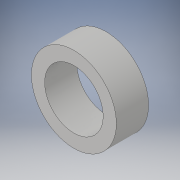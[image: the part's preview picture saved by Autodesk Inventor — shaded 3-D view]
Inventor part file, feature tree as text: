
AUTODESK INVENTOR PART (.ipt)
format: ipt  version: 2021 (Build 250183000, 183)  size: 121,344 bytes
history: native  units: mm
features: other x14, extrude x1, sketch x1
ambient origin geometry x8: Origin, YZ Plane, XZ Plane, XY Plane, X Axis, Y Axis, Z Axis, Center Point
bodies: Solid1 (feature_tree)
feature tree (16):
  extrude  "Extrusion1"  TaperAngle=0.0deg  [1 undecoded]
  other  "to_base_XY"
  other  "to_base_YZ"
  other  "to_base_ZX"
  other  "to_base_X"
  other  "to_base_Y"
  other  "to_base_Z"
  other  "to_base_Center"
  other  "to_nut_XY"
  other  "to_nut_YZ"
  other  "to_nut_ZX"
  other  "to_nut_X"
  other  "to_nut_Y"
  other  "to_nut_Z"
  other  "to_nut_Center"
  sketch  "Sketch_1"  dims[d0=5.5mm d1=0.0mm d2=0.0mm d3=0.0mm]
note: 1 required parameter value undecoded (feature->parameter linkage not recoverable at this tier; creation-order binding heuristic only, values carry confidence <= 0.55)
